# Revit family: 22L-P-I
name_source: partatom
category: Lighting Fixtures
revit_build: Autodesk Revit 2014 (Build: 20130308_1515(x64)
units: mm (PartAtom-declared; Revit-internal decimal feet)

## types (4) — shared parameters
Assembly Code = D5020200
Color Filter = 16777215
Default Elevation = 4' - 0"
Description = 22L Pendant Indirect (22L-P-I) is a small-scale extruded aluminum fixture. Its small housing provides a clean, minimalist look in both small and large areas.
Dimming Lamp Color Temperature Shift = <None>
Emit Shape Visible in Rendering = No
Emit from Rectangle Length = 0' - 2"
Features = Variable Intensity technology provides specifiable lumen output/wattage
100% indirect distribution
2 SDCM color variation
Fixture Distribution = Indirect
Glass = Glass - Hubbell - White
Housing Material = Paint - Hubbell - Matte White
Lamp = LED
Load Classification = Lighting
Manufacturer = Litecontrol Lighting
Model = 22L-P-I
Mounting = Pendant
Photometric Link = https://www.hubbell.com
Photometric Notes = More IES files download on Photometric Link
Photometric Web File = 22L-P-I-LPA-4-SOF-X-CX-35K-I100.ies
Product Documentation Link = https://hubbellcdn.com
Product Page URL = https://www.hubbell.com
Tilt Angle = -90.00°
Type Comments = Lighting Fixture
URL = https://www.hubbell.com
Voltage = 120 V
Warranty = 5-Years Warranty

## per-type parameters (varying)
| type | Apparent Load | Emit from Rectangle Width | Power Factor | Wattage Comments | zz Length 1 |
| 22L-P-I-04 | 28 VA | 3' - 10" | 1 | 28.4 | 4' - 0" |
| 22L-P-I-03 | 21 VA | 2' - 10" | 0.9 | 21 | 3' - 0" |
| 22L-P-I-06 | 43 VA | 5' - 10" | 1 | 42.6 | 6' - 0" |
| 22L-P-I-08 | 57 VA | 7' - 10" | 1 | 56.8 W | 8' - 0" |

## geometry (parser evidence)
native form markers: Sweep x2
no freeform markers — native parametric forms only
